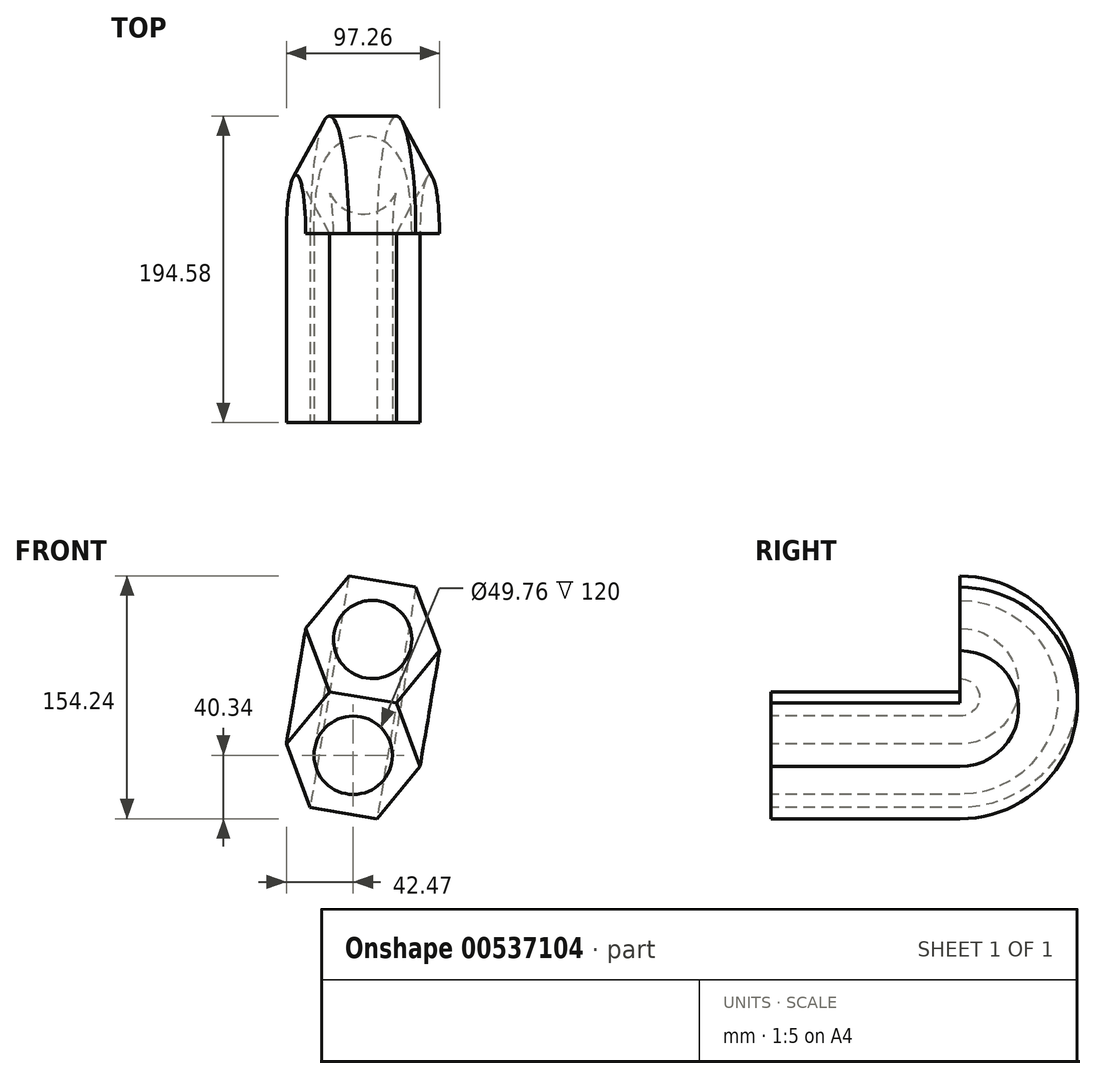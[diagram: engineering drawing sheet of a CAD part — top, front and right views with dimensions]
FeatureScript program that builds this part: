
annotation { "Feature Type Name" : "Feature", "Feature Type Description" : "" }
export const myFeature = defineFeature(function(context is Context, id is Id, definition is map)
    precondition{}
    {
        {
            var Q0;
            Q0=qCreatedBy(makeId("Front.planeOp"),FACE);
            var sketch = newSketch(context, id + "F0", { "sketchPlane" : qUnion([Q0])});
            skCircle(sketch, "E0", {"center": v(0, 0) * mm, "radius": 24.88 * mm});
            skCircle(sketch, "E1.cCircle", {"center": v(0, 0) * mm, "radius": 43.06 * mm, "construction": true});
            skLineSegment(sketch, "E1.0", {"start": v(-27.4, -33.22) * mm, "end": v(-42.47, 7.12) * mm});
            skLineSegment(sketch, "E1.1", {"start": v(-42.47, 7.12) * mm, "end": v(-15.07, 40.34) * mm});
            skLineSegment(sketch, "E1.2", {"start": v(-15.07, 40.34) * mm, "end": v(27.4, 33.22) * mm});
            skLineSegment(sketch, "E1.3", {"start": v(27.4, 33.22) * mm, "end": v(42.47, -7.12) * mm});
            skLineSegment(sketch, "E1.4", {"start": v(42.47, -7.12) * mm, "end": v(15.07, -40.34) * mm});
            skLineSegment(sketch, "E1.5", {"start": v(15.07, -40.34) * mm, "end": v(-27.4, -33.22) * mm});
            skSolve(sketch);
        }
        {
            var Q0;
            Q0 = qSketchRegion(id + "F0", true);
            var Q1;
            Q1=sQuery(id+"F0.wireOp",EDGE,"E1.2");
            var Q2;
            Q2=sQuery(id+"F0.wireOp",EDGE,"E0");
            extrude(context, id + "F1", {"entities" : qUnion([Q0]), "surfaceEntities" : qUnion([Q1, Q2]), "endBound" : BoundingType.SYMMETRIC, "oppositeDirection" : true, "depth" : 120 * mm, "offsetDistance" : 25 * mm});
        }
        {
            var Q0;
            Q0=makeQuery(id+"F1.opExtrude","CAP_FACE",FACE,{"disambiguationData":[OSD([sQuery(id+"F0.wireOp",EDGE,"E0"),sQuery(id+"F0.wireOp",EDGE,"E1.0"),sQuery(id+"F0.wireOp",EDGE,"E1.1"),sQuery(id+"F0.wireOp",EDGE,"E1.2"),sQuery(id+"F0.wireOp",EDGE,"E1.3"),sQuery(id+"F0.wireOp",EDGE,"E1.4"),sQuery(id+"F0.wireOp",EDGE,"E1.5")])],"isStart":false});
            var Q1;
            Q1=makeQuery(id+"F1.opExtrude","CAP_EDGE",EDGE,{"disambiguationData":[OSD([sQuery(id+"F0.wireOp",EDGE,"E1.2")])],"isStart":false});
            revolve(context, id + "F2", {"operationType" : NewBodyOperationType.ADD, "entities" : qUnion([Q0]), "axis" : qUnion([Q1]), "revolveType" : RevolveType.ONE_DIRECTION, "angle" : 180 * degree});
        }
    });
